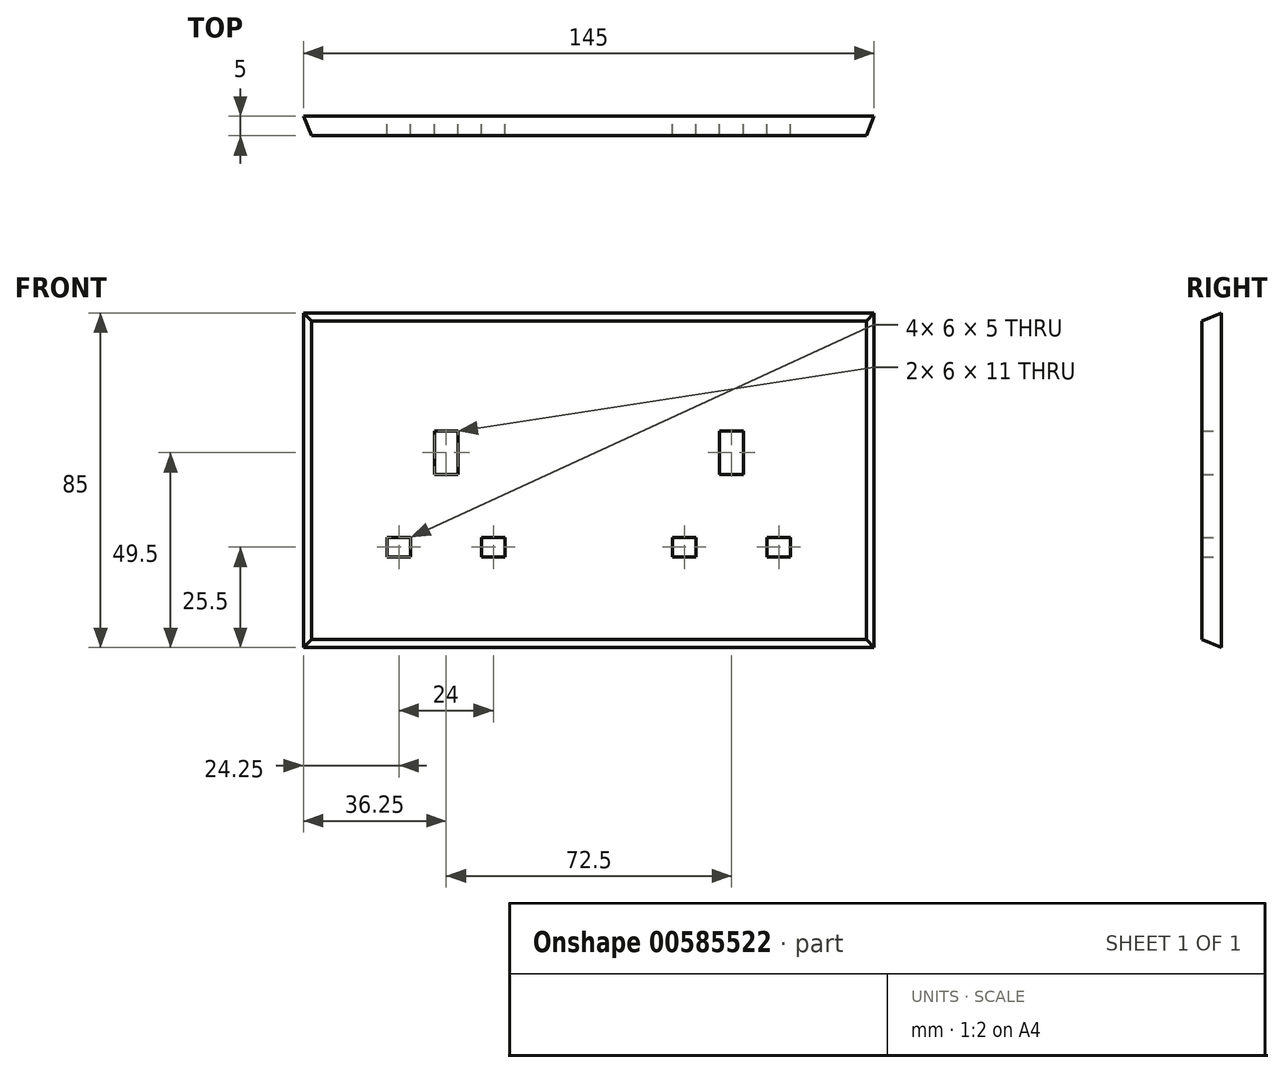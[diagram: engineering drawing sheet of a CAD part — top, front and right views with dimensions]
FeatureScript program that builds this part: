
annotation { "Feature Type Name" : "Feature", "Feature Type Description" : "" }
export const myFeature = defineFeature(function(context is Context, id is Id, definition is map)
    precondition{}
    {
        {
            var Q0;
            Q0=qCreatedBy(makeId("Front.planeOp"),FACE);
            var sketch = newSketch(context, id + "F0", { "sketchPlane" : qUnion([Q0])});
            skLineSegment(sketch, "E0.bottom", {"start": v(72.5, 42.5) * mm, "end": v(-72.5, 42.5) * mm});
            skLineSegment(sketch, "E0.top", {"start": v(72.5, -42.5) * mm, "end": v(-72.5, -42.5) * mm});
            skLineSegment(sketch, "E0.left", {"start": v(72.5, 42.5) * mm, "end": v(72.5, -42.5) * mm});
            skLineSegment(sketch, "E0.right", {"start": v(-72.5, 42.5) * mm, "end": v(-72.5, -42.5) * mm});
            skPoint(sketch, "E1.MirrorP", {"position": v(-72.5, 0) * mm});
            skSolve(sketch);
        }
        {
            var Q0;
            Q0 = qSketchRegion(id + "F0", true);
            extrude(context, id + "F1", {"entities" : qUnion([Q0]), "depth" : 5 * mm, "offsetDistance" : 25 * mm});
        }
        {
            var Q0;
            Q0=qCreatedBy(makeId("Front.planeOp"),FACE);
            var sketch = newSketch(context, id + "F2", { "sketchPlane" : qUnion([Q0])});
            skLineSegment(sketch, "E2.bottom", {"start": v(72.5, 42.5) * mm, "end": v(-72.5, 42.5) * mm, "construction": true});
            skLineSegment(sketch, "E2.top", {"start": v(72.5, -42.5) * mm, "end": v(-72.5, -42.5) * mm, "construction": true});
            skLineSegment(sketch, "E2.left", {"start": v(72.5, 42.5) * mm, "end": v(72.5, -42.5) * mm, "construction": true});
            skLineSegment(sketch, "E2.right", {"start": v(-72.5, 42.5) * mm, "end": v(-72.5, -42.5) * mm, "construction": true});
            skPoint(sketch, "E2.middle", {"position": v(0, 0) * mm});
            skLineSegment(sketch, "E3.bottom", {"start": v(-39.25, 12.5) * mm, "end": v(-33.25, 12.5) * mm});
            skLineSegment(sketch, "E3.top", {"start": v(-39.25, 1.5) * mm, "end": v(-33.25, 1.5) * mm});
            skLineSegment(sketch, "E3.left", {"start": v(-39.25, 12.5) * mm, "end": v(-39.25, 1.5) * mm});
            skLineSegment(sketch, "E3.right", {"start": v(-33.25, 12.5) * mm, "end": v(-33.25, 1.5) * mm});
            skLineSegment(sketch, "E4.bottom", {"start": v(-51.25, -19.5) * mm, "end": v(-45.25, -19.5) * mm});
            skLineSegment(sketch, "E4.top", {"start": v(-51.25, -14.5) * mm, "end": v(-45.25, -14.5) * mm});
            skLineSegment(sketch, "E4.left", {"start": v(-51.25, -19.5) * mm, "end": v(-51.25, -14.5) * mm});
            skLineSegment(sketch, "E4.right", {"start": v(-45.25, -19.5) * mm, "end": v(-45.25, -14.5) * mm});
            skLineSegment(sketch, "E5", {"start": v(-36.25, 12.5) * mm, "end": v(-36.25, 1.5) * mm, "construction": true});
            skLineSegment(sketch, "E6.MirrorCS", {"start": v(-21.25, -19.5) * mm, "end": v(-27.25, -19.5) * mm});
            skLineSegment(sketch, "E7.MirrorCS", {"start": v(-21.25, -14.5) * mm, "end": v(-27.25, -14.5) * mm});
            skLineSegment(sketch, "E8.MirrorCS", {"start": v(-21.25, -19.5) * mm, "end": v(-21.25, -14.5) * mm});
            skLineSegment(sketch, "E9.MirrorCS", {"start": v(-27.25, -19.5) * mm, "end": v(-27.25, -14.5) * mm});
            skLineSegment(sketch, "E10.MirrorCS", {"start": v(-33.25, 1.5) * mm, "end": v(-39.25, 1.5) * mm});
            skLineSegment(sketch, "E11.MirrorCS", {"start": v(-33.25, 12.5) * mm, "end": v(-39.25, 12.5) * mm});
            skPoint(sketch, "E12.MirrorP", {"position": v(-72.5, 0) * mm});
            skLineSegment(sketch, "E13.MirrorCS", {"start": v(39.25, 1.5) * mm, "end": v(33.25, 1.5) * mm});
            skLineSegment(sketch, "E14.MirrorCS", {"start": v(33.25, 12.5) * mm, "end": v(39.25, 12.5) * mm});
            skLineSegment(sketch, "E15.MirrorCS", {"start": v(51.25, -14.5) * mm, "end": v(45.25, -14.5) * mm});
            skLineSegment(sketch, "E16.MirrorCS", {"start": v(27.25, -19.5) * mm, "end": v(27.25, -14.5) * mm});
            skLineSegment(sketch, "E17.MirrorCS", {"start": v(39.25, 12.5) * mm, "end": v(39.25, 1.5) * mm});
            skLineSegment(sketch, "E18.MirrorCS", {"start": v(39.25, 12.5) * mm, "end": v(33.25, 12.5) * mm});
            skLineSegment(sketch, "E19.MirrorCS", {"start": v(21.25, -19.5) * mm, "end": v(27.25, -19.5) * mm});
            skLineSegment(sketch, "E20.MirrorCS", {"start": v(21.25, -19.5) * mm, "end": v(21.25, -14.5) * mm});
            skLineSegment(sketch, "E21.MirrorCS", {"start": v(45.25, -19.5) * mm, "end": v(45.25, -14.5) * mm});
            skLineSegment(sketch, "E22.MirrorCS", {"start": v(33.25, 1.5) * mm, "end": v(39.25, 1.5) * mm});
            skLineSegment(sketch, "E23.MirrorCS", {"start": v(21.25, -14.5) * mm, "end": v(27.25, -14.5) * mm});
            skLineSegment(sketch, "E24.MirrorCS", {"start": v(51.25, -19.5) * mm, "end": v(45.25, -19.5) * mm});
            skLineSegment(sketch, "E25.MirrorCS", {"start": v(33.25, 12.5) * mm, "end": v(33.25, 1.5) * mm});
            skLineSegment(sketch, "E26.MirrorCS", {"start": v(51.25, -19.5) * mm, "end": v(51.25, -14.5) * mm});
            skLineSegment(sketch, "E27.MirrorCS", {"start": v(36.25, 12.5) * mm, "end": v(36.25, 1.5) * mm, "construction": true});
            skSolve(sketch);
        }
        {
            var Q0;
            Q0 = qSketchRegion(id + "F2", true);
            extrude(context, id + "F3", {"entities" : qUnion([Q0]), "operationType" : NewBodyOperationType.REMOVE, "endBound" : BoundingType.UP_TO_NEXT, "depth" : 25 * mm, "offsetDistance" : 25 * mm});
        }
        {
            var Q0;
            Q0=makeQuery(id+"F1.opExtrude","CAP_EDGE",EDGE,{"disambiguationData":[OSD([sQuery(id+"F0.wireOp",EDGE,"E0.bottom")])],"isStart":false});
            var Q1;
            Q1=makeQuery(id+"F1.opExtrude","CAP_EDGE",EDGE,{"disambiguationData":[OSD([sQuery(id+"F0.wireOp",EDGE,"E0.right")])],"isStart":false});
            var Q2;
            Q2=makeQuery(id+"F1.opExtrude","CAP_EDGE",EDGE,{"disambiguationData":[OSD([sQuery(id+"F0.wireOp",EDGE,"E0.top")])],"isStart":false});
            var Q3;
            Q3=makeQuery(id+"F1.opExtrude","CAP_EDGE",EDGE,{"disambiguationData":[OSD([sQuery(id+"F0.wireOp",EDGE,"E0.left")])],"isStart":false});
            chamfer(context, id + "F4", {"entities" : qUnion([Q0, Q1, Q2, Q3]), "chamferType" : ChamferType.TWO_OFFSETS, "width1" : 2 * mm, "oppositeDirection" : false, "width2" : 5 * mm, "tangentPropagation" : true});
        }
    });
